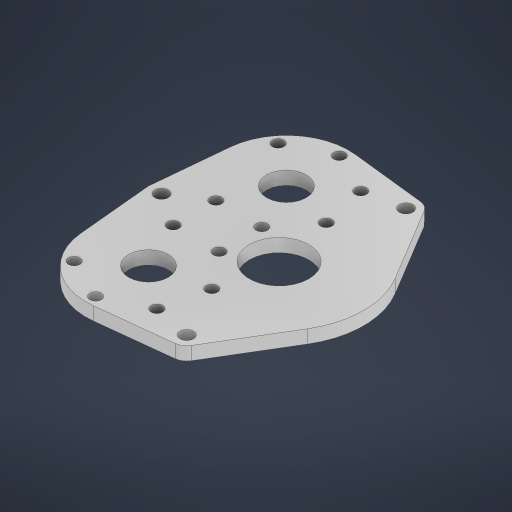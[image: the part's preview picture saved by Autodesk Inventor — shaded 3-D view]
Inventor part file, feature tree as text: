
AUTODESK INVENTOR PART (.ipt)
format: ipt  version: 2024.3 (Build 283343000, 343)  size: 265,216 bytes
history: native  units: in
note: dims shown in document units (in); Inventor stores cm internally (conversion verified against a paired STEP export)
features: extrude x1, sketch x1
ambient origin geometry x8: Origin, YZ Plane, XZ Plane, XY Plane, X Axis, Y Axis, Z Axis, Center Point
bodies: Solid1 (feature_tree)
feature tree (2):
  extrude  "Extrusion1"  Depth=0.25in
  sketch  "Sketch1"  dims[d0=0.5in d1=3.0in d2=0.5in d3=2.36in d4=2.36in d5=0.25in d6=0.1in d8=0.5in d9=0.257in d11=0.25in d12=0.5in d13=0.257in d14=0.25in d15=0.5in d16=0.257in d17=0.25in d18=0.25in d19=1.125in d20=0.75in d21=2.0in d22=0.22in d23=2.7559in d25=360.0deg d27=2.0in d28=2.7559in d30=360.0deg d32=0.25in d33=0.0in]
